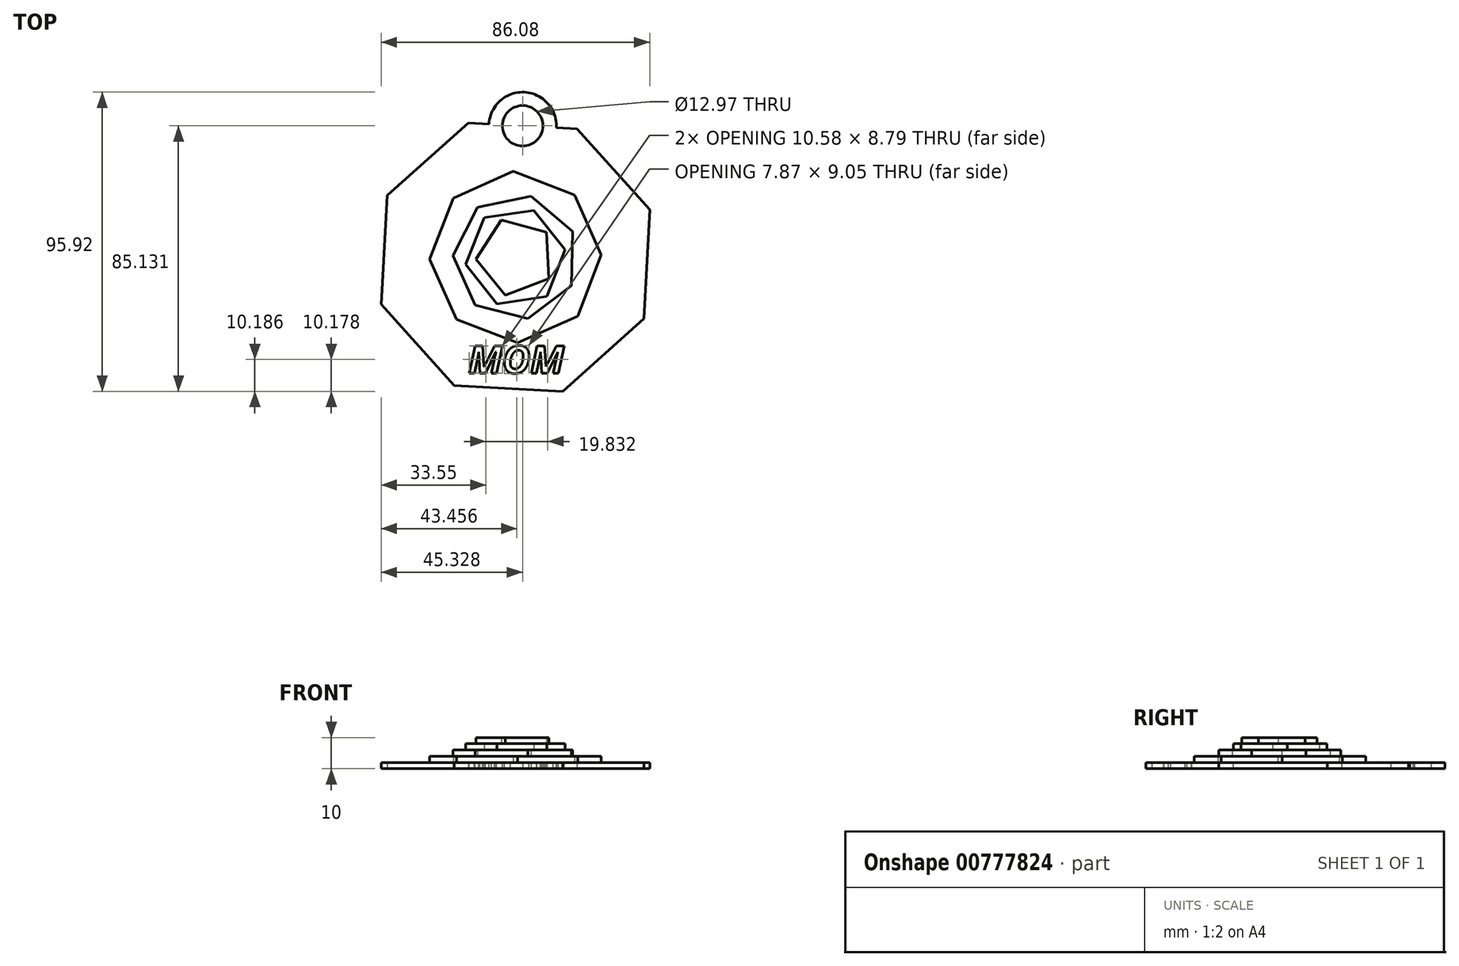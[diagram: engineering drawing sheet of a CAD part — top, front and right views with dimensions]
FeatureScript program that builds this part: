
annotation { "Feature Type Name" : "Feature", "Feature Type Description" : "" }
export const myFeature = defineFeature(function(context is Context, id is Id, definition is map)
    precondition{}
    {
        {
            var Q0;
            Q0=qCreatedBy(makeId("Top.planeOp"),FACE);
            var sketch = newSketch(context, id + "F0", { "sketchPlane" : qUnion([Q0])});
            skCircle(sketch, "E0.cCircle", {"center": v(0, 0) * mm, "radius": 42.15 * mm, "construction": true});
            skLineSegment(sketch, "E0.0", {"start": v(19.72, 41.14) * mm, "end": v(43.04, 15.15) * mm});
            skLineSegment(sketch, "E0.1", {"start": v(43.04, 15.15) * mm, "end": v(41.14, -19.72) * mm});
            skLineSegment(sketch, "E0.2", {"start": v(41.14, -19.72) * mm, "end": v(15.15, -43.04) * mm});
            skLineSegment(sketch, "E0.3", {"start": v(15.15, -43.04) * mm, "end": v(-19.72, -41.14) * mm});
            skLineSegment(sketch, "E0.4", {"start": v(-19.72, -41.14) * mm, "end": v(-43.04, -15.15) * mm});
            skLineSegment(sketch, "E0.5", {"start": v(-43.04, -15.15) * mm, "end": v(-41.14, 19.72) * mm});
            skLineSegment(sketch, "E0.6", {"start": v(-41.14, 19.72) * mm, "end": v(-15.15, 43.04) * mm});
            skLineSegment(sketch, "E0.7", {"start": v(-15.15, 43.04) * mm, "end": v(19.72, 41.14) * mm});
            skPoint(sketch, "E0.0.midPoint", {"position": v(31.38, 28.14) * mm});
            skSolve(sketch);
        }
        {
            var Q0;
            Q0=makeQuery(id+"F0.imprint","IMPRINT",FACE,{"disambiguationData":[TD([[makeQuery(id+"F0.imprint","IMPRINT",EDGE,{"derivedFrom":sQuery(id+"F0.wireOp",EDGE,"E0.0")}),-1.0]])]});
            extrude(context, id + "F1", {"entities" : qUnion([Q0]), "depth" : 2 * mm, "offsetDistance" : 25.4 * mm});
        }
        {
            var Q0;
            Q0=makeQuery(id+"F1.opExtrude","CAP_FACE",FACE,{"disambiguationData":[OSD([sQuery(id+"F0.wireOp",EDGE,"E0.0"),sQuery(id+"F0.wireOp",EDGE,"E0.1"),sQuery(id+"F0.wireOp",EDGE,"E0.2"),sQuery(id+"F0.wireOp",EDGE,"E0.3"),sQuery(id+"F0.wireOp",EDGE,"E0.4"),sQuery(id+"F0.wireOp",EDGE,"E0.5"),sQuery(id+"F0.wireOp",EDGE,"E0.6"),sQuery(id+"F0.wireOp",EDGE,"E0.7")])],"isStart":false});
            var sketch = newSketch(context, id + "F2", { "sketchPlane" : qUnion([Q0])});
            skCircle(sketch, "E1.cCircle", {"center": v(0, 0) * mm, "radius": 25.4 * mm, "construction": true});
            skLineSegment(sketch, "E1.0", {"start": v(-19.93, 18.95) * mm, "end": v(-0.7, 27.5) * mm});
            skLineSegment(sketch, "E1.1", {"start": v(-0.7, 27.5) * mm, "end": v(18.95, 19.93) * mm});
            skLineSegment(sketch, "E1.2", {"start": v(18.95, 19.93) * mm, "end": v(27.5, 0.7) * mm});
            skLineSegment(sketch, "E1.3", {"start": v(27.5, 0.7) * mm, "end": v(19.93, -18.95) * mm});
            skLineSegment(sketch, "E1.4", {"start": v(19.93, -18.95) * mm, "end": v(0.7, -27.5) * mm});
            skLineSegment(sketch, "E1.5", {"start": v(0.7, -27.5) * mm, "end": v(-18.95, -19.93) * mm});
            skLineSegment(sketch, "E1.6", {"start": v(-18.95, -19.93) * mm, "end": v(-27.5, -0.7) * mm});
            skLineSegment(sketch, "E1.7", {"start": v(-27.5, -0.7) * mm, "end": v(-19.93, 18.95) * mm});
            skPoint(sketch, "E1.0.midPoint", {"position": v(-10.31, 23.22) * mm});
            skSolve(sketch);
        }
        {
            var Q0;
            Q0 = qSketchRegion(id + "F2", true);
            extrude(context, id + "F3", {"entities" : qUnion([Q0]), "operationType" : NewBodyOperationType.ADD, "depth" : 2 * mm, "offsetDistance" : 25.4 * mm});
        }
        {
            var Q0;
            Q0=makeQuery(id+"F3.opExtrude","CAP_FACE",FACE,{"disambiguationData":[OSD([sQuery(id+"F2.wireOp",EDGE,"E1.0"),sQuery(id+"F2.wireOp",EDGE,"E1.1"),sQuery(id+"F2.wireOp",EDGE,"E1.2"),sQuery(id+"F2.wireOp",EDGE,"E1.3"),sQuery(id+"F2.wireOp",EDGE,"E1.4"),sQuery(id+"F2.wireOp",EDGE,"E1.5"),sQuery(id+"F2.wireOp",EDGE,"E1.6"),sQuery(id+"F2.wireOp",EDGE,"E1.7")])],"isStart":false});
            var sketch = newSketch(context, id + "F4", { "sketchPlane" : qUnion([Q0])});
            skCircle(sketch, "E2.cCircle", {"center": v(0, 0) * mm, "radius": 18.1 * mm, "construction": true});
            skLineSegment(sketch, "E2.0", {"start": v(-20.08, 0.5) * mm, "end": v(-12.13, 16.02) * mm});
            skLineSegment(sketch, "E2.1", {"start": v(-12.13, 16.02) * mm, "end": v(4.96, 19.47) * mm});
            skLineSegment(sketch, "E2.2", {"start": v(4.96, 19.47) * mm, "end": v(18.32, 8.26) * mm});
            skLineSegment(sketch, "E2.3", {"start": v(18.32, 8.26) * mm, "end": v(17.87, -9.17) * mm});
            skLineSegment(sketch, "E2.4", {"start": v(17.87, -9.17) * mm, "end": v(3.97, -19.7) * mm});
            skLineSegment(sketch, "E2.5", {"start": v(3.97, -19.7) * mm, "end": v(-12.92, -15.39) * mm});
            skLineSegment(sketch, "E2.6", {"start": v(-12.92, -15.39) * mm, "end": v(-20.08, 0.5) * mm});
            skPoint(sketch, "E2.0.midPoint", {"position": v(-16.1, 8.26) * mm});
            skSolve(sketch);
        }
        {
            var Q0;
            Q0 = qSketchRegion(id + "F4", true);
            extrude(context, id + "F5", {"entities" : qUnion([Q0]), "operationType" : NewBodyOperationType.ADD, "depth" : 2 * mm, "offsetDistance" : 25.4 * mm});
        }
        {
            var Q0;
            Q0=makeQuery(id+"F5.opExtrude","CAP_FACE",FACE,{"disambiguationData":[OSD([sQuery(id+"F4.wireOp",EDGE,"E2.0"),sQuery(id+"F4.wireOp",EDGE,"E2.1"),sQuery(id+"F4.wireOp",EDGE,"E2.2"),sQuery(id+"F4.wireOp",EDGE,"E2.3"),sQuery(id+"F4.wireOp",EDGE,"E2.4"),sQuery(id+"F4.wireOp",EDGE,"E2.5"),sQuery(id+"F4.wireOp",EDGE,"E2.6")])],"isStart":false});
            var sketch = newSketch(context, id + "F6", { "sketchPlane" : qUnion([Q0])});
            skSolve(sketch);
        }
        {
            var Q0;
            Q0=makeQuery(id+"F6.imprint","IMPRINT",FACE,{"disambiguationData":[TD([[makeQuery(id+"F6.imprint","IMPRINT",EDGE,{"derivedFrom":makeQuery(id+"F5.opExtrude","CAP_EDGE",EDGE,{"disambiguationData":[OSD([sQuery(id+"F4.wireOp",EDGE,"E2.0")])],"isStart":false})}),-1.0]])]});
            var sketch = newSketch(context, id + "F7", { "sketchPlane" : qUnion([Q0])});
            skCircle(sketch, "E3.cCircle", {"center": v(0, 0) * mm, "radius": 13.94 * mm, "construction": true});
            skLineSegment(sketch, "E3.0", {"start": v(-15.93, -2.36) * mm, "end": v(-10, 12.61) * mm});
            skLineSegment(sketch, "E3.1", {"start": v(-10, 12.61) * mm, "end": v(5.92, 14.97) * mm});
            skLineSegment(sketch, "E3.2", {"start": v(5.92, 14.97) * mm, "end": v(15.93, 2.36) * mm});
            skLineSegment(sketch, "E3.3", {"start": v(15.93, 2.36) * mm, "end": v(10, -12.61) * mm});
            skLineSegment(sketch, "E3.4", {"start": v(10, -12.61) * mm, "end": v(-5.92, -14.97) * mm});
            skLineSegment(sketch, "E3.5", {"start": v(-5.92, -14.97) * mm, "end": v(-15.93, -2.36) * mm});
            skPoint(sketch, "E3.0.midPoint", {"position": v(-12.97, 5.13) * mm});
            skSolve(sketch);
        }
        {
            var Q0;
            Q0 = qSketchRegion(id + "F7", true);
            extrude(context, id + "F8", {"entities" : qUnion([Q0]), "operationType" : NewBodyOperationType.ADD, "depth" : 2 * mm, "offsetDistance" : 25.4 * mm});
        }
        {
            var Q0;
            Q0=makeQuery(id+"F8.opExtrude","CAP_FACE",FACE,{"disambiguationData":[OSD([sQuery(id+"F7.wireOp",EDGE,"E3.0"),sQuery(id+"F7.wireOp",EDGE,"E3.1"),sQuery(id+"F7.wireOp",EDGE,"E3.2"),sQuery(id+"F7.wireOp",EDGE,"E3.3"),sQuery(id+"F7.wireOp",EDGE,"E3.4"),sQuery(id+"F7.wireOp",EDGE,"E3.5")])],"isStart":false});
            var sketch = newSketch(context, id + "F9", { "sketchPlane" : qUnion([Q0])});
            skCircle(sketch, "E4.cCircle", {"center": v(0, 0) * mm, "radius": 10.29 * mm, "construction": true});
            skLineSegment(sketch, "E4.0", {"start": v(-12.7, -0.66) * mm, "end": v(-4.55, 11.88) * mm});
            skLineSegment(sketch, "E4.1", {"start": v(-4.55, 11.88) * mm, "end": v(9.89, 8) * mm});
            skLineSegment(sketch, "E4.2", {"start": v(9.89, 8) * mm, "end": v(10.66, -6.93) * mm});
            skLineSegment(sketch, "E4.3", {"start": v(10.66, -6.93) * mm, "end": v(-3.3, -12.28) * mm});
            skLineSegment(sketch, "E4.4", {"start": v(-3.3, -12.28) * mm, "end": v(-12.7, -0.66) * mm});
            skPoint(sketch, "E4.0.midPoint", {"position": v(-8.63, 5.6) * mm});
            skSolve(sketch);
        }
        {
            var Q0;
            Q0 = qSketchRegion(id + "F9", true);
            extrude(context, id + "F10", {"entities" : qUnion([Q0]), "operationType" : NewBodyOperationType.ADD, "depth" : 2 * mm, "offsetDistance" : 25.4 * mm});
        }
        {
            var Q0;
            Q0=makeQuery(id+"F1.opExtrude","CAP_FACE",FACE,{"disambiguationData":[OSD([sQuery(id+"F0.wireOp",EDGE,"E0.0"),sQuery(id+"F0.wireOp",EDGE,"E0.1"),sQuery(id+"F0.wireOp",EDGE,"E0.2"),sQuery(id+"F0.wireOp",EDGE,"E0.3"),sQuery(id+"F0.wireOp",EDGE,"E0.4"),sQuery(id+"F0.wireOp",EDGE,"E0.5"),sQuery(id+"F0.wireOp",EDGE,"E0.6"),sQuery(id+"F0.wireOp",EDGE,"E0.7")])],"isStart":false});
            var sketch = newSketch(context, id + "F11", { "sketchPlane" : qUnion([Q0])});
            skCircle(sketch, "E5", {"center": v(2.29, 42.1) * mm, "radius": 10.8 * mm});
            skSolve(sketch);
        }
        {
            var Q0;
            Q0 = qSketchRegion(id + "F11", true);
            extrude(context, id + "F12", {"entities" : qUnion([Q0]), "operationType" : NewBodyOperationType.ADD, "oppositeDirection" : true, "depth" : 2 * mm, "offsetDistance" : 25.4 * mm});
        }
        {
            var Q0;
            Q0=makeQuery(id+"F12.boolean.opBoolean","MERGE",FACE,{"derivedFrom":[makeQuery(id+"F1.opExtrude","CAP_FACE",FACE,{"disambiguationData":[OSD([sQuery(id+"F0.wireOp",EDGE,"E0.0"),sQuery(id+"F0.wireOp",EDGE,"E0.1"),sQuery(id+"F0.wireOp",EDGE,"E0.2"),sQuery(id+"F0.wireOp",EDGE,"E0.3"),sQuery(id+"F0.wireOp",EDGE,"E0.4"),sQuery(id+"F0.wireOp",EDGE,"E0.5"),sQuery(id+"F0.wireOp",EDGE,"E0.6"),sQuery(id+"F0.wireOp",EDGE,"E0.7")])],"isStart":false}),makeQuery(id+"F12.opExtrude","CAP_FACE",FACE,{"disambiguationData":[OSD([sQuery(id+"F11.wireOp",EDGE,"E5")])],"isStart":true})]});
            var sketch = newSketch(context, id + "F13", { "sketchPlane" : qUnion([Q0])});
            skCircle(sketch, "E6", {"center": v(2.29, 42.1) * mm, "radius": 6.48 * mm});
            skSolve(sketch);
        }
        {
            var Q0;
            Q0 = qSketchRegion(id + "F13", true);
            extrude(context, id + "F14", {"entities" : qUnion([Q0]), "operationType" : NewBodyOperationType.REMOVE, "oppositeDirection" : true, "depth" : 25.4 * mm, "offsetDistance" : 25.4 * mm});
        }
        {
            var Q0;
            Q0=makeQuery(id+"F12.boolean.opBoolean","MERGE",FACE,{"derivedFrom":[makeQuery(id+"F1.opExtrude","CAP_FACE",FACE,{"disambiguationData":[OSD([sQuery(id+"F0.wireOp",EDGE,"E0.0"),sQuery(id+"F0.wireOp",EDGE,"E0.1"),sQuery(id+"F0.wireOp",EDGE,"E0.2"),sQuery(id+"F0.wireOp",EDGE,"E0.3"),sQuery(id+"F0.wireOp",EDGE,"E0.4"),sQuery(id+"F0.wireOp",EDGE,"E0.5"),sQuery(id+"F0.wireOp",EDGE,"E0.6"),sQuery(id+"F0.wireOp",EDGE,"E0.7")])],"isStart":false}),makeQuery(id+"F12.opExtrude","CAP_FACE",FACE,{"disambiguationData":[OSD([sQuery(id+"F11.wireOp",EDGE,"E5")])],"isStart":true})]});
            var sketch = newSketch(context, id + "F15", { "sketchPlane" : qUnion([Q0])});
            skText(sketch, "E7", { "text": "MOM", "fontName": "OpenSans-BoldItalic.ttf"});
            const initialGuessF15  = {"E7": [-0.0151, -0.03726, 1, 0, 0.00887]};
            skSetInitialGuess(sketch, initialGuessF15);
            skSolve(sketch);
        }
        {
            var Q0;
            Q0 = qSketchRegion(id + "F15", true);
            extrude(context, id + "F16", {"entities" : qUnion([Q0]), "operationType" : NewBodyOperationType.REMOVE, "oppositeDirection" : true, "depth" : 25.4 * mm, "offsetDistance" : 25.4 * mm});
        }
    });
